# Revit family: Grohe_ThermostatForConcealed_102167KF00
name_source: partatom
category: Plumbing Fixtures
units: mm (PartAtom-declared; Revit-internal decimal feet)

## family parameters
Cut with Voids When Loaded = No
Host = Face
OmniClass Number = 23.45.05.00
OmniClass Title = Sanitary Equipment
Part Type = Normal
Room Calculation Point = No
Round Connector Dimension = Use Diameter
Shared = No

## types (1)
- Thermostat For Concealed (102167KF00)
    Assembly Code = D2013
    AssetType = Fixed
    BIMObjectName = Grohe_ThermostatForConcealed_102167KF00
    CO2NeutralProduction = GROHE is one of the first leading manufacturer within the sanitary industry having a CO2-neutral production.
    ClassificationName = Uniclass2015
    ClassificationValue = Pr_40_20_87_55
    Color = Grohe_Black
    Cost = 0 $
    Default Elevation = 0 mm  [stored 0 ft]
    Description = Thermostat For Concealed
    DimensionsDocumentLink = https://cdn.cloud.grohe.com
    DocumentationCertificates = https://www.bimstore.co
    DocumentationInstallationGuide = https://www.bimstore.co
    DocumentationLiterature = https://www.bimstore.co
    DocumentationMaintenance = https://www.bimstore.co
    DocumentationTechnical = https://www.bimstore.co
    DurationUnit = Years
    Ecojoy = No
    ExpectedLife = 0
    Finish = Black
    FullRecyclabilityOfPlastic = All plastic components are fully recycable
    GROHESocialCommittment = green.grohe.com/social_engagement
    GROHESustainability = green.grohe.com
    IfcExportAs = IfcPipeFitting
    IfcExportType = IfcPipeFittingType
    Keynote = N16
    Manufacturer = Grohe
    ManufacturerName = Grohe
    Model = Thermostat For Concealed
    ModelNumber = 102167KF00
    ModelReference = Thermostat For Concealed
    NBSDescription = Shower fittings package
    NBSObjectName = Grohe - Shower fittings package
    NBSReference = 45-35-70/254
    NominalDepth = 0 mm  [stored 0 ft]
    NominalHeight = 0 mm  [stored 0 ft]
    NominalLength = 0 mm  [stored 0 ft]
    PQDiagramLink = https://cdn.cloud.grohe.com
    PrimaryMaterial = Grohe_Black
    ProductDescription = set for final installation for GROHE Rapido SmartBox (35 600/35 604)

metal wall escutcheon with GROHE FastFixation (covered escutcheon and shaft sealing, covered fixing), retroactively 6° adjustable

GROHE Long-Life finish

GROHE SmartControl push for ON-OFF, turn for volume adjustment from GROHE Water Saving to Full Flow, exchangeable symbols

GROHE TurboStat compact cartridge with wax thermoelement

GROHE ProGrip with knurl structure

GROHE SafeStop safety button at 38°C

GROHE SafeStop Plus optional temperature limiter at 43°C or 46°C included

built-in non return valves and dirt strainers

multiple outlets can be run simultaneously

without roughing-in set

flow performance: outlet A = 23 l/min, outlet B = 27 l/min, outlet C = 23 l/min, outlet A + B = 33 l/min, outlet A + B + C = 36 l/min
    ProductNumber = 102167KF00
    ProductShortText = Thermostat for concealed installation with 3 valves
    ProductType = Thermostat
    ProductionYear = 2023
    SustainabilityAward = green.grohe.com/awards
    SustainabilityReport = green.grohe.com/reporting
    TPIDocumentLink = https://cdn.cloud.grohe.com
    Type Comments = Thermostat For Concealed
    TypeName = Thermostat For Concealed
    URL = https://www.grohe.co.uk
    WarrantyDurationLabor = 0
    WarrantyDurationParts = 0
    WarrantyDurationUnit = Years
    _BSBibleVersion = 17
    _BimSpecGuid = 0
    _CurrentRevision = 1
    _DistributedBy = https://www.bimstore.co
    _ObjectUserGuide = https://www.bimstore.co

note: [stored X ft] marks values corroborated as IEEE doubles in the binary element streams (Revit-internal decimal feet)

## geometry (parser evidence)
native form markers: Sweep x1
no freeform markers — native parametric forms only
